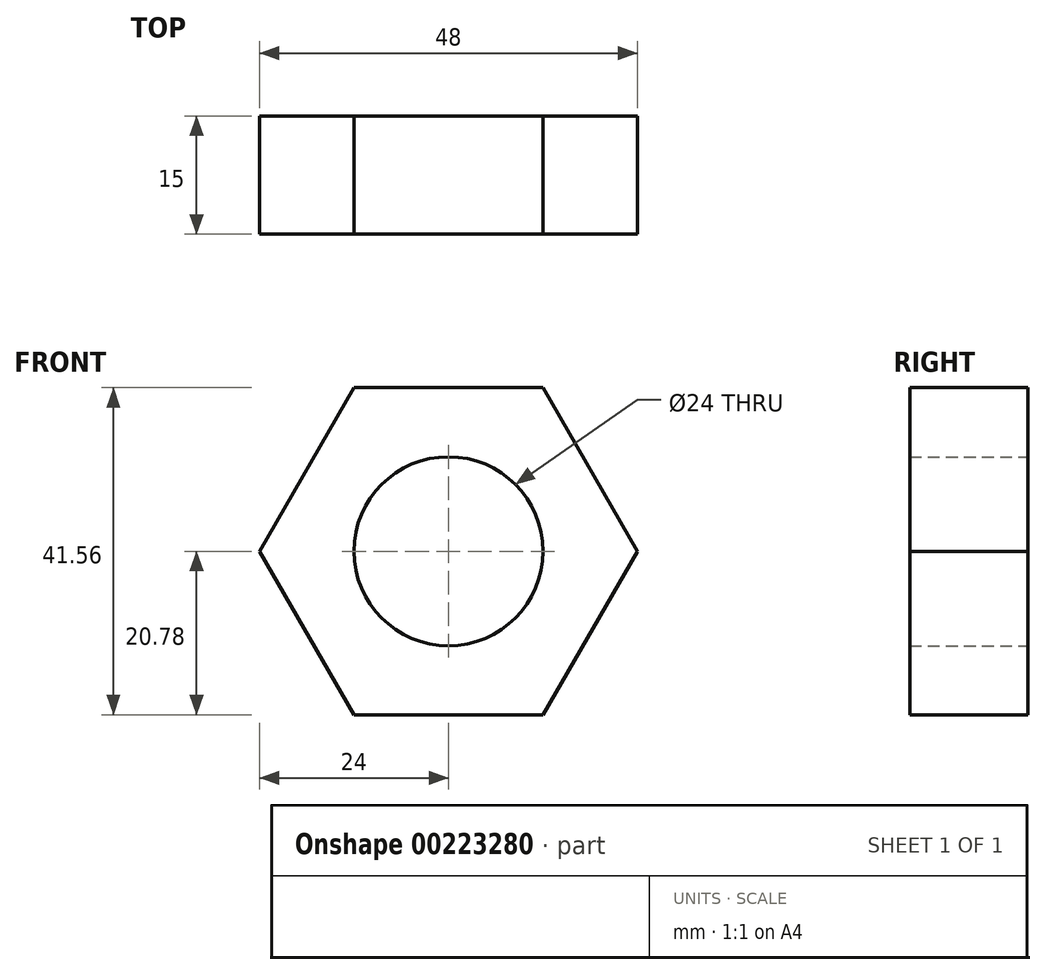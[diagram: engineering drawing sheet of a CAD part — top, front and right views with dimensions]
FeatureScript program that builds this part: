
annotation { "Feature Type Name" : "Feature", "Feature Type Description" : "" }
export const myFeature = defineFeature(function(context is Context, id is Id, definition is map)
    precondition{}
    {
        {
            var Q0;
            Q0=qCreatedBy(makeId("Front.planeOp"),FACE);
            var sketch = newSketch(context, id + "F0", { "sketchPlane" : qUnion([Q0])});
            skCircle(sketch, "E0.cCircle", {"center": v(0, 0) * mm, "radius": 20.78 * mm, "construction": true});
            skLineSegment(sketch, "E0.0", {"start": v(24, 0) * mm, "end": v(12, -20.78) * mm});
            skLineSegment(sketch, "E0.1", {"start": v(12, -20.78) * mm, "end": v(-12, -20.78) * mm});
            skLineSegment(sketch, "E0.2", {"start": v(-12, -20.78) * mm, "end": v(-24, 0) * mm});
            skLineSegment(sketch, "E0.3", {"start": v(-24, 0) * mm, "end": v(-12, 20.78) * mm});
            skLineSegment(sketch, "E0.4", {"start": v(-12, 20.78) * mm, "end": v(12, 20.78) * mm});
            skLineSegment(sketch, "E0.5", {"start": v(12, 20.78) * mm, "end": v(24, 0) * mm});
            skPoint(sketch, "E0.0.midPoint", {"position": v(18, -10.4) * mm});
            skCircle(sketch, "E1", {"center": v(0, 0) * mm, "radius": 12 * mm});
            skSolve(sketch);
        }
        {
            var Q0;
            Q0=makeQuery(id+"F0.imprint","IMPRINT",FACE,{"disambiguationData":[TD([[makeQuery(id+"F0.imprint","IMPRINT",EDGE,{"derivedFrom":sQuery(id+"F0.wireOp",EDGE,"E0.0")}),-1.0]])]});
            extrude(context, id + "F1", {"entities" : qUnion([Q0]), "depth" : 15 * mm});
        }
    });
